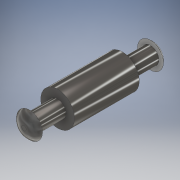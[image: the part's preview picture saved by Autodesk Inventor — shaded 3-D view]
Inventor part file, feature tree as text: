
AUTODESK INVENTOR PART (.ipt)
format: ipt  version: 2017 (Build 210142000, 142)  size: 144,384 bytes
history: native  units: mm
features: extrude x5, sketch x5, fillet x2
ambient origin geometry x8: Origin, YZ Plane, XZ Plane, XY Plane, X Axis, Y Axis, Z Axis, Center Point
bodies: Body1 (feature_tree)
feature tree (12):
  extrude  "Extrusion2"  Depth=11.5mm TaperAngle=0.0deg
  extrude  "Extrusion3"  Depth=5.0mm TaperAngle=0.0deg
  extrude  "Extrusion4"  Depth=5.0mm TaperAngle=0.0deg
  extrude  "Extrusion5"  Depth=1.0mm TaperAngle=0.0deg
  extrude  "Extrusion6"  Depth=1.0mm TaperAngle=0.0deg
  fillet  "Fillet2"  Radius=2.3mm
  fillet  "Fillet3"  Radius=2.3mm
  sketch  "Sketch2"  dims[d3=6.0mm d4=11.5mm d5=0.0mm]
  sketch  "Sketch3"  dims[d6=3.0mm d7=5.0mm d8=0.0mm]
  sketch  "Sketch7"  dims[d16=3.0mm d17=5.0mm d18=0.0mm]
  sketch  "Sketch8"  dims[d23=4.6mm d24=1.0mm d25=0.0mm]
  sketch  "Sketch9"  dims[d26=4.6mm d27=1.0mm d28=0.0mm d29=2.3mm d30=2.3mm]
